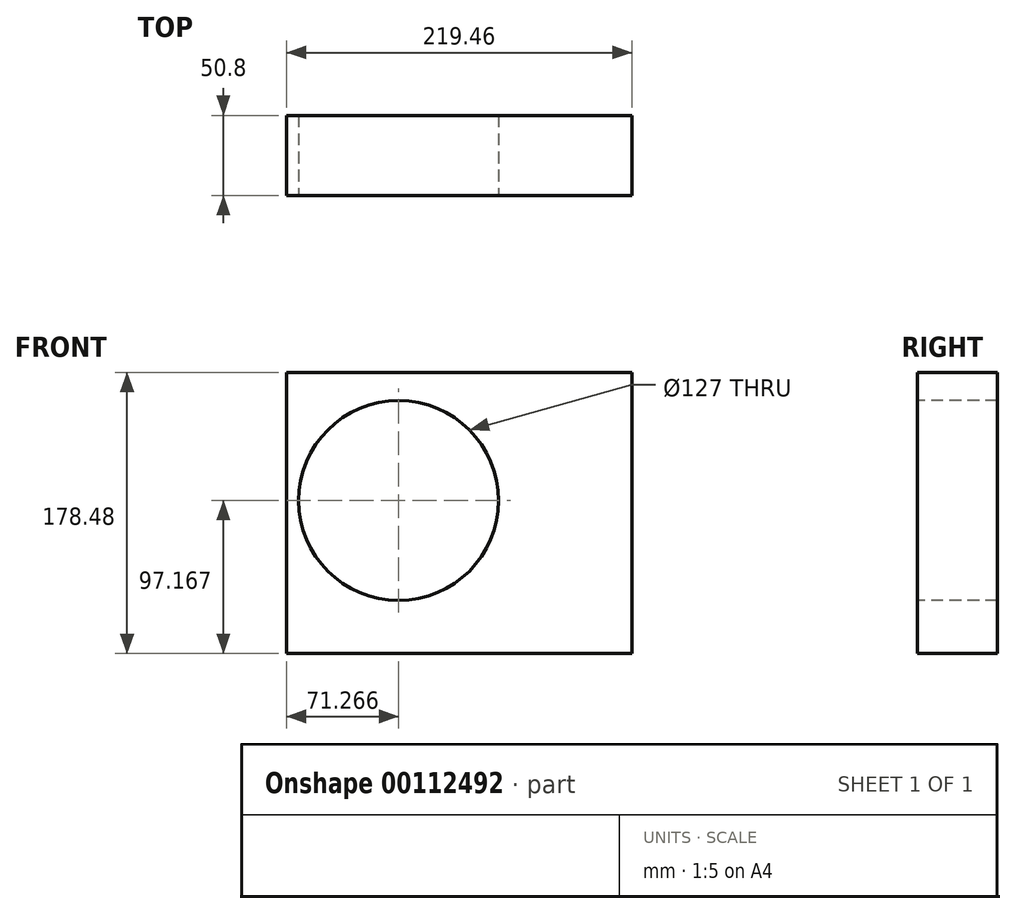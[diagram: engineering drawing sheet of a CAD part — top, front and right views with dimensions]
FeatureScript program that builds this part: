
annotation { "Feature Type Name" : "Feature", "Feature Type Description" : "" }
export const myFeature = defineFeature(function(context is Context, id is Id, definition is map)
    precondition{}
    {
        {
            var Q0;
            Q0=qCreatedBy(makeId("Front.planeOp"),FACE);
            var sketch = newSketch(context, id + "F0", { "sketchPlane" : qUnion([Q0])});
            skLineSegment(sketch, "E0.bottom", {"start": v(-121.28, 88.61) * mm, "end": v(98.18, 88.61) * mm});
            skLineSegment(sketch, "E0.top", {"start": v(-121.28, -89.87) * mm, "end": v(98.18, -89.87) * mm});
            skLineSegment(sketch, "E0.left", {"start": v(-121.28, 88.61) * mm, "end": v(-121.28, -89.87) * mm});
            skLineSegment(sketch, "E0.right", {"start": v(98.18, 88.61) * mm, "end": v(98.18, -89.87) * mm});
            skSolve(sketch);
        }
        {
            var Q0;
            Q0=makeQuery(id+"F0.imprint","IMPRINT",FACE,{"disambiguationData":[TD([[makeQuery(id+"F0.imprint","IMPRINT",EDGE,{"derivedFrom":sQuery(id+"F0.wireOp",EDGE,"E0.bottom")}),-1.0]])]});
            extrude(context, id + "F1", {"entities" : qUnion([Q0]), "depth" : 50.8 * mm});
        }
        {
            var Q0;
            Q0=makeQuery(id+"F1.opExtrude","CAP_FACE",FACE,{"disambiguationData":[OSD([sQuery(id+"F0.wireOp",EDGE,"E0.bottom"),sQuery(id+"F0.wireOp",EDGE,"E0.top"),sQuery(id+"F0.wireOp",EDGE,"E0.left"),sQuery(id+"F0.wireOp",EDGE,"E0.right")])],"isStart":false});
            var sketch = newSketch(context, id + "F2", { "sketchPlane" : qUnion([Q0])});
            skCircle(sketch, "E1", {"center": v(-50.01, 7.3) * mm, "radius": 21.16 * mm});
            skSolve(sketch);
        }
        {
            var Q0;
            Q0=sQuery(id+"F2.wireOp",VERTEX,"E1.center");
            var Q1;
            Q1=makeQuery(id+"F1.opExtrude","SWEPT_BODY",BODY,{"disambiguationData":[OSD([sQuery(id+"F0.wireOp",EDGE,"E0.bottom"),sQuery(id+"F0.wireOp",EDGE,"E0.top"),sQuery(id+"F0.wireOp",EDGE,"E0.left"),sQuery(id+"F0.wireOp",EDGE,"E0.right")])]});
            hole(context, id + "F3", {"style" : HoleStyle.SIMPLE, "endStyle" : HoleEndStyle.THROUGH, "holeDiameter" : 127 * mm, "locations" : qUnion([Q0]), "scope" : qUnion([Q1]), "isTappedThrough" : true});
        }
    });
